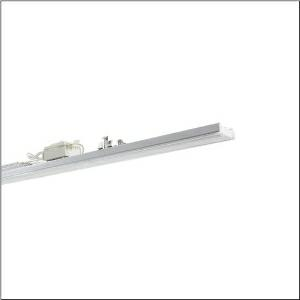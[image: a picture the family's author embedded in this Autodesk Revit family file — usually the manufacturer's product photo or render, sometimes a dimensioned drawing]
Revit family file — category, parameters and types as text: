
# Revit family: licross_11_recessed_mo_51tl14dn425g
name_source: partatom
category: Lighting Fixtures
units: mm (PartAtom-declared; Revit-internal decimal feet)

## family parameters
Cut with Voids When Loaded = No
Host = Face
Light Source = No
Part Type = Normal
Room Calculation Point = No
Round Connector Dimension = Use Diameter
Shared = No

## types (1)
- --- (1 x LED, 2600 lm, 15.2 W, 4000K)
    Apparent Load = 15 VA
    CIE Flux Codes = 56 84 97 100 100
    Color Rendering = 80
    Color Temperature = 4000K
    Default Elevation = 1800 mm
    Description = Licross 11 Recessed MO, luminaire insert, of sheet steel, coil coated, white, length: 1.500mm, width: 66mm, height: 67mm, LED rated luminous flux: 2.600lm, light colour: 840, SDCM (Standard Deviation of Colour Matching)MacAdam ≤ 2 SDCM (initial), control gear: DALI 2, with plug, 5-pole, with phase selection, mains connection: 220..240V, AC, 50/60Hz, rated input power: 15.2W, internal wiring halogen-free, primary light control with lens, of plastic, primary optical cover: cover, of PMMA, light emission: direct distribution, primary light characteristic: asymmetric, protection rating (complete): IP40, insulation class (complete): insulation class I (protective earthing), certification: CE, ENEC, VDE, UKCA, protection symbol: D if used in an environment without relevant dust loads with corresponding accessories, impact resistance: IK06, permissible ambient temperature for indoor applications: -25..+50°C, corresponds to IFS (International Featured Standards) requirements for safety and quality in the food industry, reducing of maximum allowable ambient temperature of 5°C with ceiling mounting, LABS conformity tested according to VDMA 24364:2018-05, The light source and the operating device comply with the requirements of the Ecodesign Regulation (EU) 2019/2020 and are replaceable in accordance with this regulation, packaging unit: 1 piece
    Height = 58 mm
    Lamp = 1 x LED
    Lamp Light Flux = 2600 lm
    Lamp Power = 15.2 W
    Lamp count = 1
    Length = 1500 mm
    Luminous efficacy = 171 lm/W
    Manufacturer = Siteco
    ModVariant = No
    Model = 51TL14DN425G
    Mounting Place = Ceiling
    Mounting Type = Pendant
    Number of Poles = 1
    OnlyDefault = Yes
    Power Factor = 1
    Product Name = Licross 11 Recessed MO
    Product group = luminaire insert | ceiling pendant
    ProductGroupID = 901
    Protection Class = Protection class I
    Protection Degree = IP 40
    RLX_Detail_Level = 1
    RLX_Emergency_Light_Flux = 0 lm
    RLX_Emergency_Type = 0
    RLX_Emergency_Type_DB = No
    RlxData = <blob elided: 24501 chars, md5=d838531e>
    Socket = socket
    Standby Power = 0 W
    System Light Flux = 2600 lm
    System Power = 15 W
    Type Comments = factory setting: luminous flux: 100 % | dim-lin: 254 | 98 mA
    Type Image = l_1296930.jpg
    URL = http://relux.com
    VarID = @adj_075467
    Voltage = 0 V
    Weight = 0.00 kg
    Width = 66 mm

## geometry (parser evidence)
native form markers: Blend x4, Sweep x11
no freeform markers — native parametric forms only
